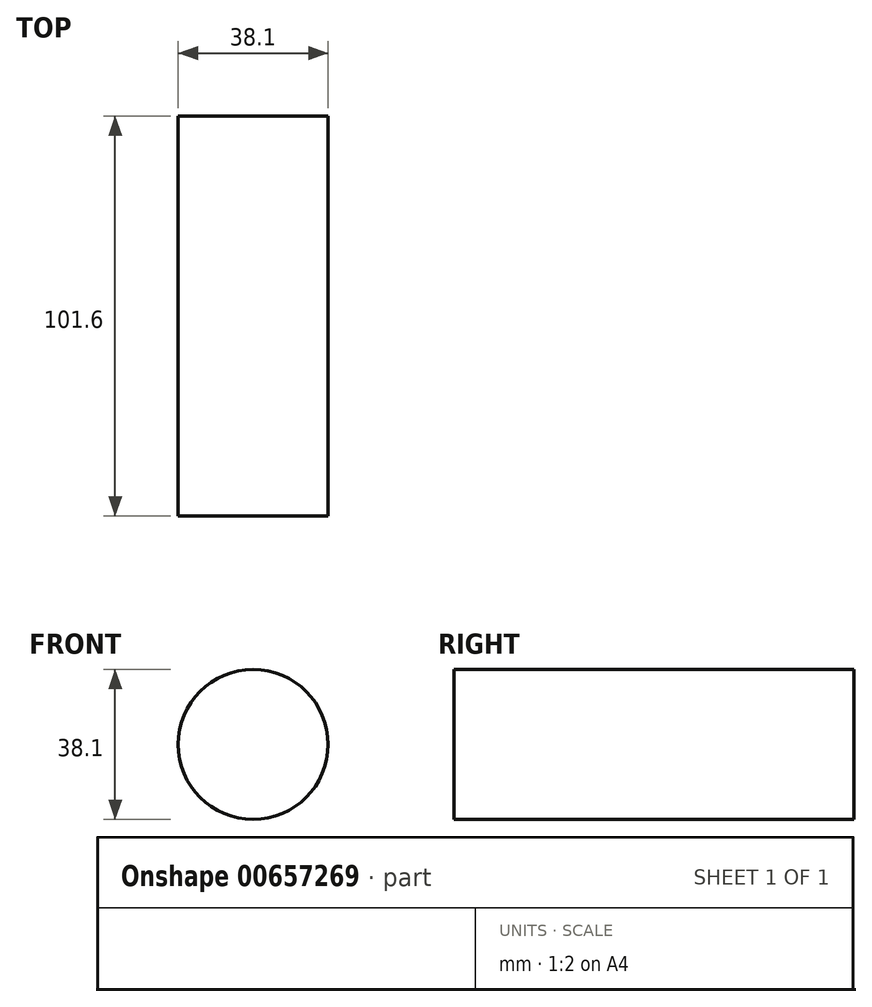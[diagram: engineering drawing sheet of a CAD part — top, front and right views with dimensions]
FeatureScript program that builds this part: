
annotation { "Feature Type Name" : "Feature", "Feature Type Description" : "" }
export const myFeature = defineFeature(function(context is Context, id is Id, definition is map)
    precondition{}
    {
        {
            var Q0;
            Q0=qCreatedBy(makeId("Front.planeOp"),FACE);
            var sketch = newSketch(context, id + "F0", { "sketchPlane" : qUnion([Q0])});
            skCircle(sketch, "E0", {"center": v(0, 0) * mm, "radius": 19.05 * mm});
            skSolve(sketch);
        }
        {
            var Q0;
            Q0=makeQuery(id+"F0.imprint","IMPRINT",FACE,{"disambiguationData":[TD([[makeQuery(id+"F0.imprint","IMPRINT",EDGE,{"derivedFrom":sQuery(id+"F0.wireOp",EDGE,"E0")}),1.0]])]});
            extrude(context, id + "F1", {"entities" : qUnion([Q0]), "endBound" : BoundingType.SYMMETRIC, "depth" : 101.6 * mm, "offsetDistance" : 25.4 * mm});
        }
        {
            var Q0;
            Q0=qCreatedBy(makeId("Top.planeOp"),FACE);
            var sketch = newSketch(context, id + "F2", { "sketchPlane" : qUnion([Q0])});
            skLineSegment(sketch, "E1", {"start": v(0, -51.17) * mm, "end": v(0, 71.38) * mm});
            skSolve(sketch);
        }
    });
